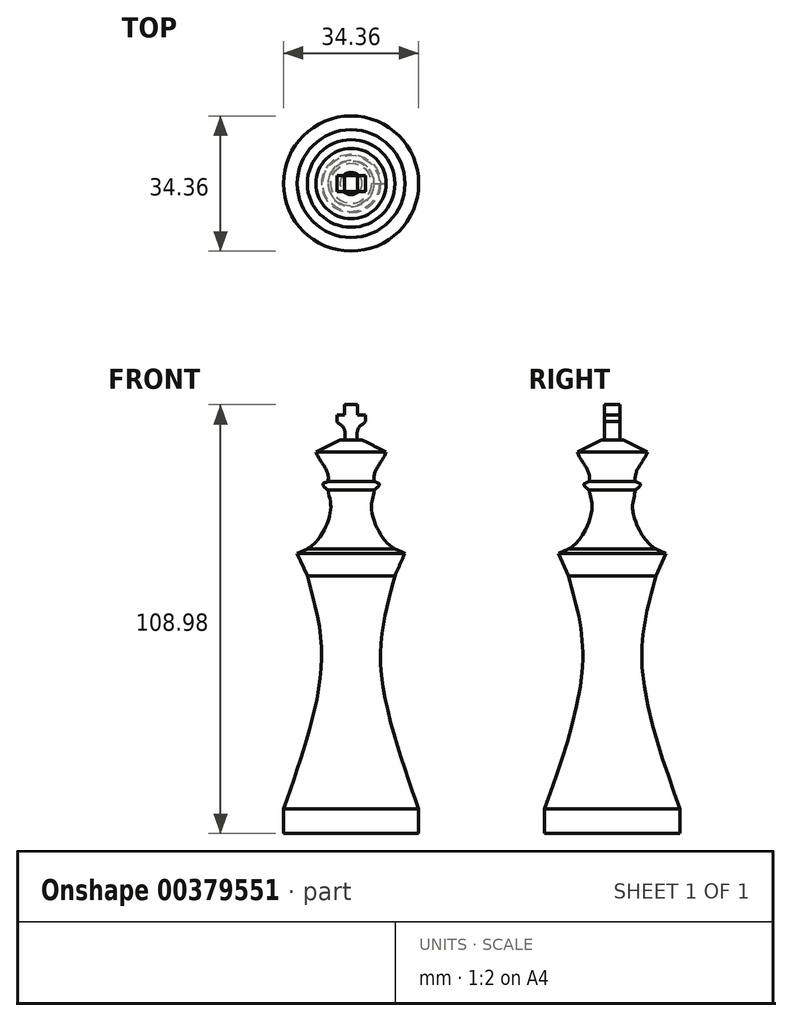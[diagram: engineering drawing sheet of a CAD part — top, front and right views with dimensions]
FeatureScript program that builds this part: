
annotation { "Feature Type Name" : "Feature", "Feature Type Description" : "" }
export const myFeature = defineFeature(function(context is Context, id is Id, definition is map)
    precondition{}
    {
        {
            var Q0;
            Q0=qCreatedBy(makeId("Front.planeOp"),FACE);
            var sketch = newSketch(context, id + "F0", { "sketchPlane" : qUnion([Q0])});
            skLineSegment(sketch, "E0.bottom", {"start": v(-17.18, -42.85) * mm, "end": v(17.18, -42.85) * mm});
            skLineSegment(sketch, "E0.top", {"start": v(-17.18, -36.6) * mm, "end": v(17.18, -36.6) * mm});
            skLineSegment(sketch, "E0.left", {"start": v(-17.18, -42.85) * mm, "end": v(-17.18, -36.6) * mm});
            skLineSegment(sketch, "E0.right", {"start": v(17.18, -42.85) * mm, "end": v(17.18, -36.6) * mm});
            skPoint(sketch, "E0.middle", {"position": v(0, -39.73) * mm});
            skLineSegment(sketch, "E1", {"start": v(0, 67.15) * mm, "end": v(0, -57.22) * mm});
            skFitSpline(sketch, "E2", {"points": [v(-17.18, -36.6) * mm, v(-7.54, 0) * mm, v(-11.1, 22.66) * mm], "startDerivative": vector(17.81, 50.87) * mm, "endDerivative": vector(-10.27, 41.77) * mm});
            skFitSpline(sketch, "E3", {"points": [v(-11.1, 29.5) * mm, v(-5.24, 39.04) * mm, v(-5.87, 44.44) * mm], "startDerivative": vector(16.4, 8.86) * mm, "endDerivative": vector(-2.58, 15.72) * mm});
            skFitSpline(sketch, "E4", {"points": [v(-5.87, 46.64) * mm, v(-8.92, 54.05) * mm], "startDerivative": vector(1.8, 8.24) * mm, "endDerivative": vector(-2.94, 7.58) * mm});
            skLineSegment(sketch, "E5", {"start": v(-8.92, 54.05) * mm, "end": v(-2.8, 57.2) * mm});
            skLineSegment(sketch, "E6", {"start": v(-2.8, 57.2) * mm, "end": v(0, 57.2) * mm});
            skFitSpline(sketch, "E7", {"points": [v(-1.59, 57.2) * mm, v(-1.9, 60.26) * mm, v(-3.6, 61.81) * mm], "startDerivative": vector(0.5, 5.1) * mm, "endDerivative": vector(-3.17, 4.41) * mm});
            skLineSegment(sketch, "E8", {"start": v(-3.6, 61.81) * mm, "end": v(-3.6, 63.5) * mm});
            skLineSegment(sketch, "E9", {"start": v(-3.6, 63.5) * mm, "end": v(-1.62, 63.5) * mm});
            skLineSegment(sketch, "E10", {"start": v(-1.62, 63.5) * mm, "end": v(-1.62, 66.13) * mm});
            skLineSegment(sketch, "E11", {"start": v(-1.62, 66.13) * mm, "end": v(0, 66.13) * mm});
            skFitSpline(sketch, "E12", {"points": [v(-5.87, 44.44) * mm, v(-7.2, 45.9) * mm, v(-5.87, 46.64) * mm], "startDerivative": vector(-3.43, 2.33) * mm, "endDerivative": vector(3.45, 2.13) * mm});
            skLineSegment(sketch, "E13.MirrorCS", {"start": v(1.62, 66.13) * mm, "end": v(0, 66.13) * mm});
            skLineSegment(sketch, "E14.MirrorCS", {"start": v(1.62, 63.5) * mm, "end": v(1.62, 66.13) * mm});
            skLineSegment(sketch, "E15.MirrorCS", {"start": v(3.6, 61.81) * mm, "end": v(3.6, 63.5) * mm});
            skFitSpline(sketch, "E16.MirrorCS", {"points": [v(1.59, 57.2) * mm, v(1.9, 60.26) * mm, v(3.6, 61.81) * mm], "startDerivative": vector(-0.5, 5.1) * mm, "endDerivative": vector(3.17, 4.41) * mm});
            skLineSegment(sketch, "E17.MirrorCS", {"start": v(3.6, 63.5) * mm, "end": v(1.62, 63.5) * mm});
            skLineSegment(sketch, "E18.MirrorCS", {"start": v(2.8, 57.2) * mm, "end": v(0, 57.2) * mm});
            skLineSegment(sketch, "E19", {"start": v(-11.1, 22.66) * mm, "end": v(-13.69, 28.38) * mm});
            skLineSegment(sketch, "E20", {"start": v(-13.69, 28.38) * mm, "end": v(-11.1, 29.5) * mm});
            skSolve(sketch);
        }
        {
            var Q0;
            {var subQ0=sQuery(id+"F0.wireOp",EDGE,"E0.left");Q0=makeQuery(id+"F0.imprint","IMPRINT",FACE,{"disambiguationData":[TD([[makeQuery(id+"F0.imprint","IMPRINT",EDGE,{"derivedFrom":subQ0}),-1.0]])]});}
            var Q1;
            {var subQ1=sQuery(id+"F0.wireOp",EDGE,"E2");Q1=makeQuery(id+"F0.imprint","IMPRINT",FACE,{"disambiguationData":[TD([[makeQuery(id+"F0.imprint","IMPRINT",EDGE,{"derivedFrom":subQ1}),-1.0]])]});}
            var Q2;
            Q2=sQuery(id+"F0.wireOp",EDGE,"E1");
            revolve(context, id + "F1", {"entities" : qUnion([Q0, Q1]), "axis" : qUnion([Q2]), "revolveType" : RevolveType.FULL});
        }
        {
            var Q0;
            {var subQ0=sQuery(id+"F0.wireOp",EDGE,"E7");Q0=makeQuery(id+"F0.imprint","IMPRINT",FACE,{"disambiguationData":[TD([[makeQuery(id+"F0.imprint","IMPRINT",EDGE,{"derivedFrom":subQ0}),-1.0]])]});}
            var Q1;
            {var subQ0=sQuery(id+"F0.wireOp",EDGE,"E13.MirrorCS");Q1=makeQuery(id+"F0.imprint","IMPRINT",FACE,{"disambiguationData":[TD([[makeQuery(id+"F0.imprint","IMPRINT",EDGE,{"derivedFrom":subQ0}),1.0]])]});}
            extrude(context, id + "F2", {"entities" : qUnion([Q0, Q1]), "operationType" : NewBodyOperationType.ADD, "endBound" : BoundingType.SYMMETRIC, "depth" : 4 * mm});
        }
    });
